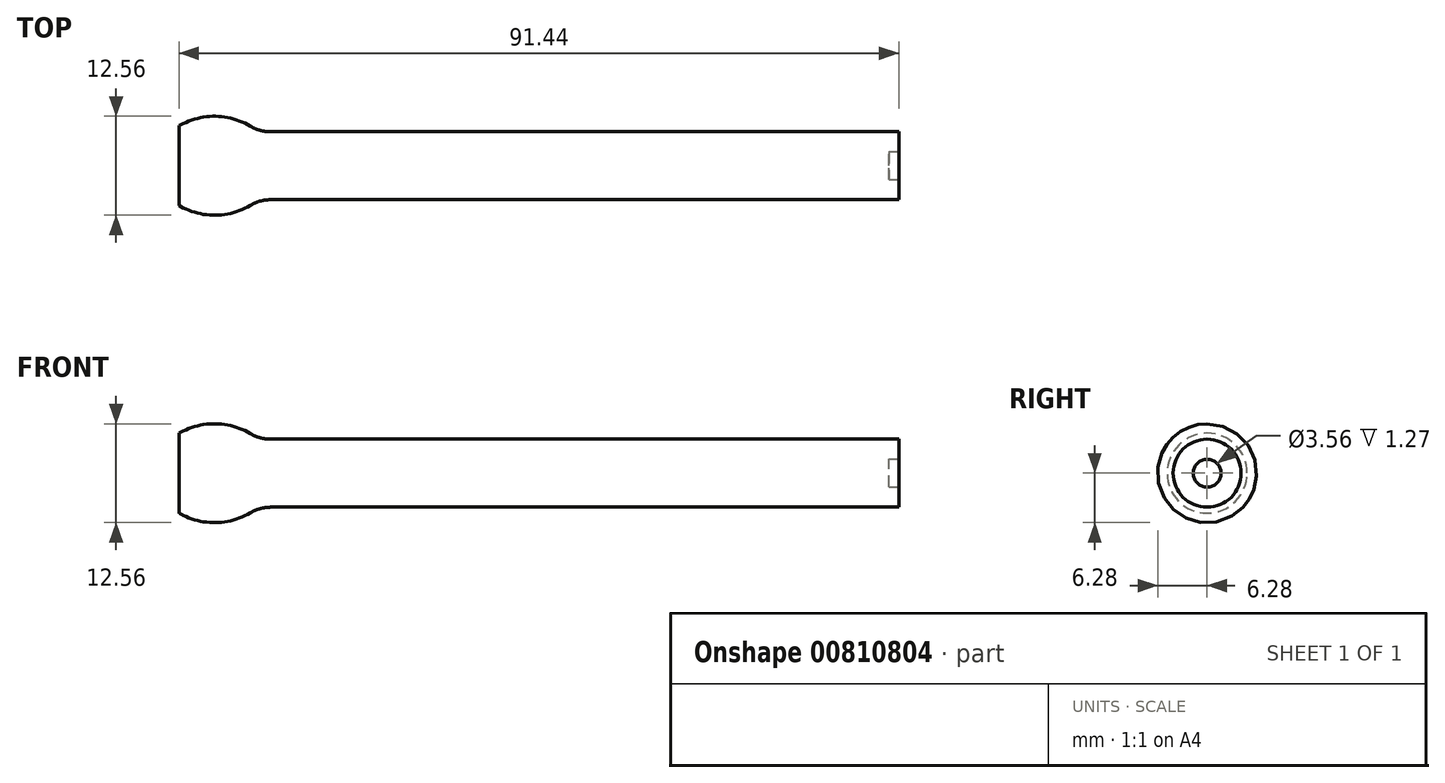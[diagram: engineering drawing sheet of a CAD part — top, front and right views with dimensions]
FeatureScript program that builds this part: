
annotation { "Feature Type Name" : "Feature", "Feature Type Description" : "" }
export const myFeature = defineFeature(function(context is Context, id is Id, definition is map)
    precondition{}
    {
        {
            var Q0;
            Q0=qCreatedBy(makeId("Right.planeOp"),FACE);
            var sketch = newSketch(context, id + "F0", { "sketchPlane" : qUnion([Q0])});
            skCircle(sketch, "E0", {"center": v(0, 0) * mm, "radius": 4.32 * mm});
            skSolve(sketch);
        }
        {
            var Q0;
            Q0 = qSketchRegion(id + "F0", true);
            extrude(context, id + "F1", {"entities" : qUnion([Q0]), "depth" : 81.28 * mm, "offsetDistance" : 25.4 * mm});
        }
        {
            var Q0;
            Q0=makeQuery(id+"F1.opExtrude","CAP_FACE",FACE,{"disambiguationData":[OSD([sQuery(id+"F0.wireOp",EDGE,"E0")])],"isStart":false});
            var sketch = newSketch(context, id + "F2", { "sketchPlane" : qUnion([Q0])});
            skCircle(sketch, "E1", {"center": v(0, 0) * mm, "radius": 1.78 * mm});
            skSolve(sketch);
        }
        {
            var Q0;
            Q0 = qSketchRegion(id + "F2", true);
            extrude(context, id + "F3", {"entities" : qUnion([Q0]), "operationType" : NewBodyOperationType.REMOVE, "oppositeDirection" : true, "depth" : 1.27 * mm, "offsetDistance" : 25.4 * mm});
        }
        {
            var Q0;
            Q0=qCreatedBy(makeId("Right.planeOp"),FACE);
            cPlane(context, id + "F4", {"entities" : qUnion([Q0]), "cplaneType" : CPlaneType.OFFSET, "offset" : 5.08 * mm, "oppositeDirection" : true, "width" : 152.4 * mm, "height" : 152.4 * mm});
        }
        {
            var Q0;
            Q0=qCreatedBy(id+"F4.planeOp",FACE);
            var sketch = newSketch(context, id + "F5", { "sketchPlane" : qUnion([Q0])});
            skCircle(sketch, "E2", {"center": v(0, 0) * mm, "radius": 7.62 * mm});
            skSolve(sketch);
        }
        {
            var Q1;
            Q1=makeQuery(id+"F0.imprint","IMPRINT",FACE,{"disambiguationData":[TD([[makeQuery(id+"F0.imprint","IMPRINT",EDGE,{"derivedFrom":sQuery(id+"F0.wireOp",EDGE,"E0")}),1.0]])]});
            var Q2;
            Q2 = qSketchRegion(id + "F5", true);
            loft(context, id + "F6", {"operationType" : NewBodyOperationType.ADD, "sheetProfilesArray" : [{ "sheetProfileEntities" : qUnion([Q1]) }, { "sheetProfileEntities" : qUnion([Q2]) }]});
        }
        {
            var Q0;
            Q0=qCreatedBy(id+"F4.planeOp",FACE);
            cPlane(context, id + "F7", {"entities" : qUnion([Q0]), "cplaneType" : CPlaneType.OFFSET, "offset" : 5.08 * mm, "oppositeDirection" : true, "width" : 152.4 * mm, "height" : 152.4 * mm});
        }
        {
            var Q0;
            Q0=qCreatedBy(id+"F7.planeOp",FACE);
            var sketch = newSketch(context, id + "F8", { "sketchPlane" : qUnion([Q0])});
            skCircle(sketch, "E3", {"center": v(0, 0) * mm, "radius": 5.08 * mm});
            skSolve(sketch);
        }
        {
            var Q1;
            Q1=makeQuery(id+"F6.opLoft","CAP_FACE",FACE,{"disambiguationData":[OSD([makeQuery(id+"F5.imprint","IMPRINT",FACE,{"disambiguationData":[TD([[makeQuery(id+"F5.imprint","IMPRINT",EDGE,{"derivedFrom":sQuery(id+"F5.wireOp",EDGE,"E2")}),1.0]])]})])],"isStart":true});
            var Q2;
            Q2 = qSketchRegion(id + "F8", true);
            loft(context, id + "F9", {"operationType" : NewBodyOperationType.ADD, "sheetProfilesArray" : [{ "sheetProfileEntities" : qUnion([Q1]) }, { "sheetProfileEntities" : qUnion([Q2]) }]});
        }
        {
            var Q0;
            {var subQ0=sQuery(id+"F5.wireOp",EDGE,"E2");Q0=makeQuery(id+"F9.boolean.opBoolean","MERGE",EDGE,{"derivedFrom":[makeQuery(id+"F6.opLoft","MID_CAP_EDGE",EDGE,{"disambiguationData":[OSD([subQ0])],"capPos":1.0}),makeQuery(id+"F9.opLoft","MID_CAP_EDGE",EDGE,{"disambiguationData":[OSD([subQ0])],"capPos":0.0})]});}
            fillet(context, id + "F10", {"entities" : qUnion([Q0]), "radius" : 8.9 * mm, "tangentPropagation" : true, "allowEdgeOverflow" : false});
        }
        {
            var Q0;
            {var subQ0=sQuery(id+"F0.wireOp",EDGE,"E0");Q0=makeQuery(id+"F6.boolean.opBoolean","MERGE",EDGE,{"derivedFrom":[makeQuery(id+"F1.opExtrude","CAP_EDGE",EDGE,{"disambiguationData":[OSD([subQ0])],"isStart":true}),makeQuery(id+"F6.opLoft","MID_CAP_EDGE",EDGE,{"disambiguationData":[OSD([subQ0])],"capPos":0.0})]});}
            fillet(context, id + "F11", {"entities" : qUnion([Q0]), "radius" : 5.08 * mm, "tangentPropagation" : true, "allowEdgeOverflow" : false});
        }
    });
